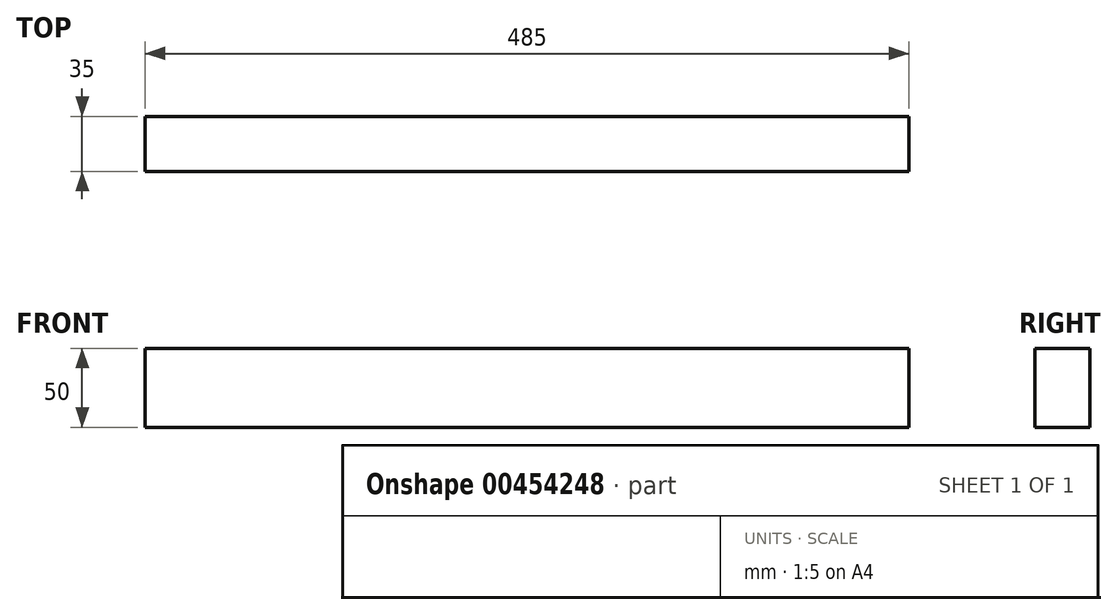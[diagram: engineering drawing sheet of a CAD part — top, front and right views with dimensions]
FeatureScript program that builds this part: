
annotation { "Feature Type Name" : "Feature", "Feature Type Description" : "" }
export const myFeature = defineFeature(function(context is Context, id is Id, definition is map)
    precondition{}
    {
        {
            var Q0;
            Q0=qCreatedBy(makeId("Front.planeOp"),FACE);
            var sketch = newSketch(context, id + "F0", { "sketchPlane" : qUnion([Q0])});
            skLineSegment(sketch, "E0.bottom", {"start": v(-242.5, 25) * mm, "end": v(242.5, 25) * mm});
            skLineSegment(sketch, "E0.top", {"start": v(-242.5, -25) * mm, "end": v(242.5, -25) * mm});
            skLineSegment(sketch, "E0.left", {"start": v(-242.5, 25) * mm, "end": v(-242.5, -25) * mm});
            skLineSegment(sketch, "E0.right", {"start": v(242.5, 25) * mm, "end": v(242.5, -25) * mm});
            skPoint(sketch, "E0.middle", {"position": v(0, 0) * mm});
            skSolve(sketch);
        }
        {
            var Q0;
            Q0=makeQuery(id+"F0.imprint","IMPRINT",FACE,{"disambiguationData":[TD([[makeQuery(id+"F0.imprint","IMPRINT",EDGE,{"derivedFrom":sQuery(id+"F0.wireOp",EDGE,"E0.bottom")}),-1.0]])]});
            extrude(context, id + "F1", {"entities" : qUnion([Q0]), "depth" : 35 * mm});
        }
    });
